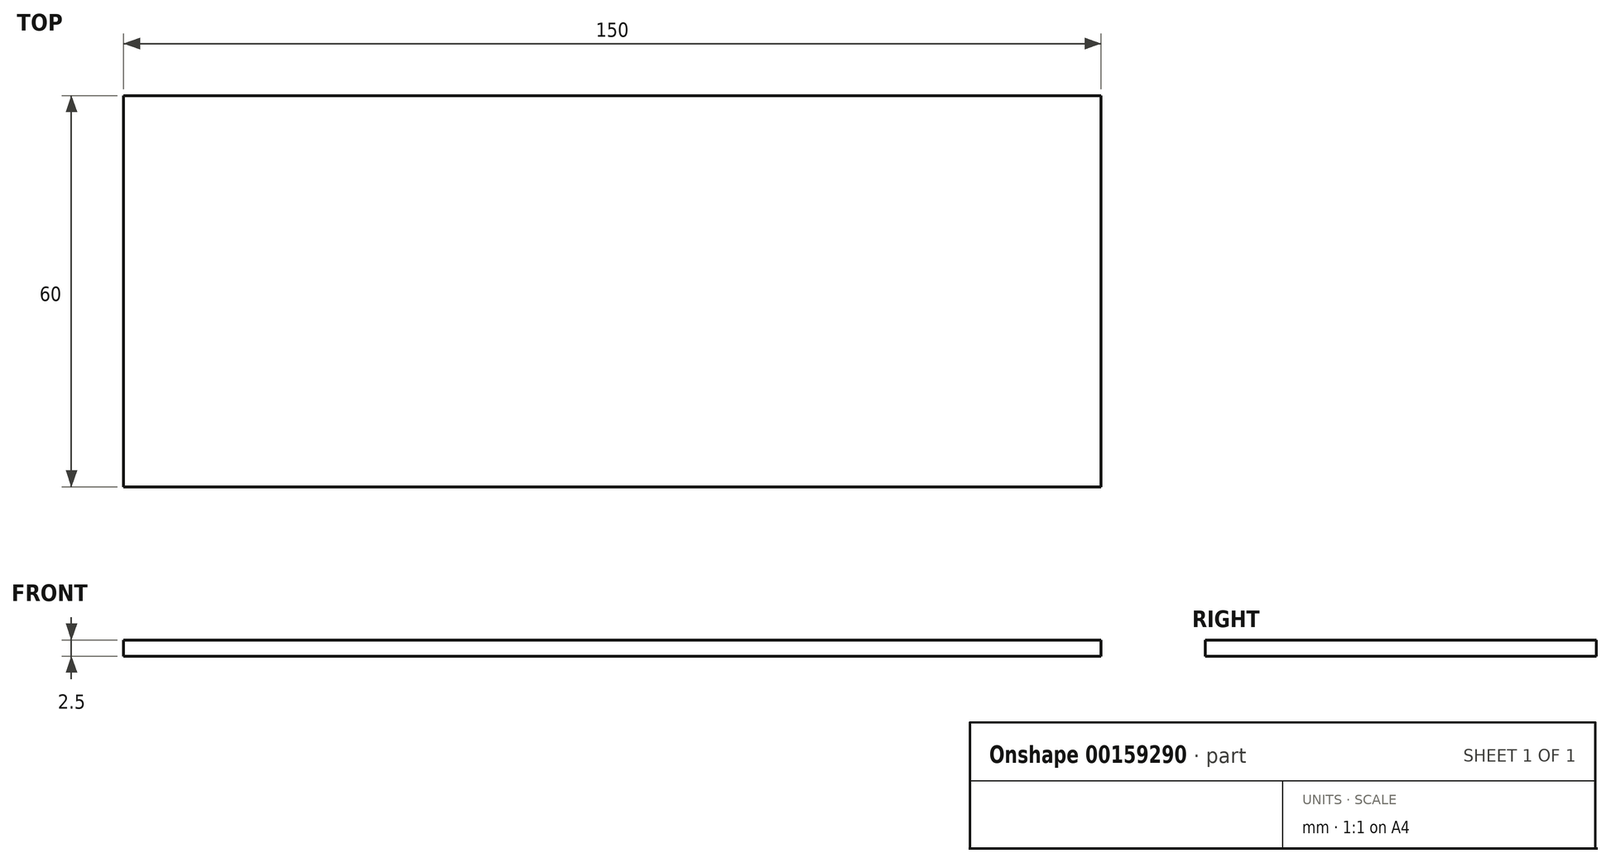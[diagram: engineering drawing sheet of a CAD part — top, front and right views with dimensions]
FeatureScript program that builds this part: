
annotation { "Feature Type Name" : "Feature", "Feature Type Description" : "" }
export const myFeature = defineFeature(function(context is Context, id is Id, definition is map)
    precondition{}
    {
        {
            var Q0;
            Q0=qCreatedBy(makeId("Top.planeOp"),FACE);
            var sketch = newSketch(context, id + "F0", { "sketchPlane" : qUnion([Q0])});
            skLineSegment(sketch, "E0.bottom", {"start": v(0, 0) * mm, "end": v(150, 0) * mm});
            skLineSegment(sketch, "E0.top", {"start": v(0, -60) * mm, "end": v(150, -60) * mm});
            skLineSegment(sketch, "E0.left", {"start": v(0, 0) * mm, "end": v(0, -60) * mm});
            skLineSegment(sketch, "E0.right", {"start": v(150, 0) * mm, "end": v(150, -60) * mm});
            skSolve(sketch);
        }
        {
            var Q0;
            Q0=makeQuery(id+"F0.imprint","IMPRINT",FACE,{"disambiguationData":[TD([[makeQuery(id+"F0.imprint","IMPRINT",EDGE,{"derivedFrom":sQuery(id+"F0.wireOp",EDGE,"E0.bottom")}),-1.0]])]});
            extrude(context, id + "F1", {"entities" : qUnion([Q0]), "depth" : 2.5 * mm});
        }
    });
